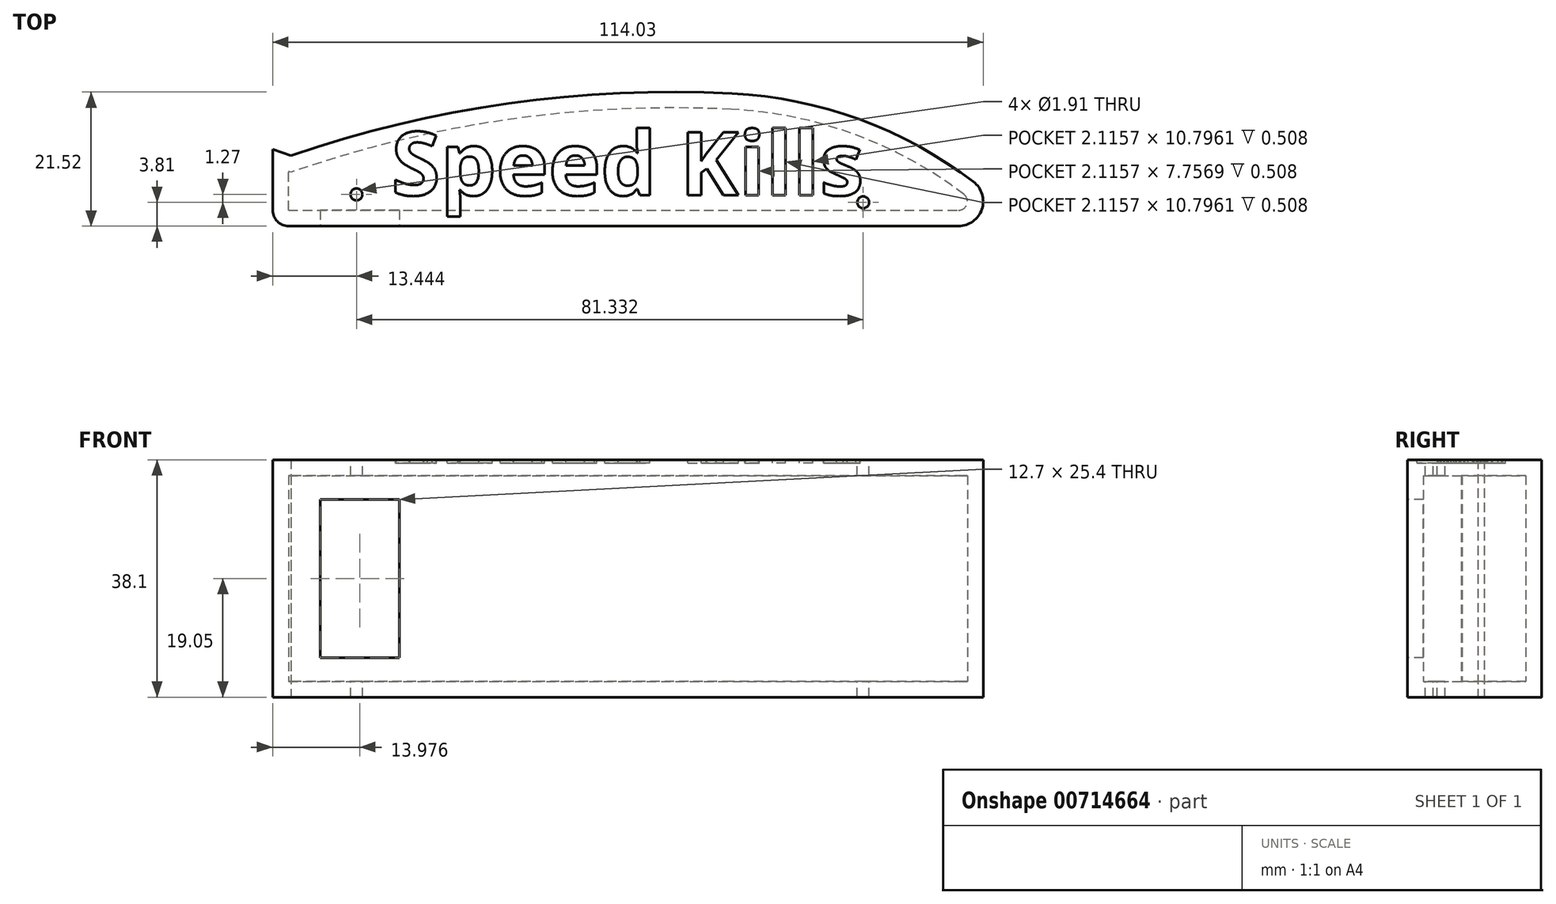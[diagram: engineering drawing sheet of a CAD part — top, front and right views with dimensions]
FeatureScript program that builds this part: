
annotation { "Feature Type Name" : "Feature", "Feature Type Description" : "" }
export const myFeature = defineFeature(function(context is Context, id is Id, definition is map)
    precondition{}
    {
        {
            var Q0;
            Q0=qCreatedBy(makeId("Top.planeOp"),FACE);
            var sketch = newSketch(context, id + "F0", { "sketchPlane" : qUnion([Q0])});
            skLineSegment(sketch, "E0", {"start": v(2.54, 0) * mm, "end": v(110.08, 0) * mm});
            skLineSegment(sketch, "E1", {"start": v(0, 2.54) * mm, "end": v(0, 10.3) * mm});
            skPoint(sketch, "E2.visualSharp", {"position": v(0, 0) * mm});
            skArc(sketch, "E2.filletArc", {"start": v(0, 2.54) * mm, "mid": v(0.74, 0.74) * mm, "end": v(2.54, 0) * mm});
            skArc(sketch, "E3", {"start": v(112.48, 7.1) * mm, "mid": v(94.19, 17.13) * mm, "end": v(73.75, 21.28) * mm});
            skArc(sketch, "E4", {"start": v(73.75, 21.28) * mm, "mid": v(36.33, 19.45) * mm, "end": v(0, 10.3) * mm});
            skArc(sketch, "E5", {"start": v(110.08, 0) * mm, "mid": v(113.83, 2.7) * mm, "end": v(112.48, 7.1) * mm});
            skSolve(sketch);
        }
        {
            var Q0;
            Q0=makeQuery(id+"F0.imprint","IMPRINT",FACE,{"disambiguationData":[TD([[makeQuery(id+"F0.imprint","IMPRINT",EDGE,{"derivedFrom":sQuery(id+"F0.wireOp",EDGE,"E0")}),1.0]])]});
            extrude(context, id + "F1", {"entities" : qUnion([Q0]), "depth" : 38.1 * mm, "offsetDistance" : 25.4 * mm});
        }
        {
            var Q0;
            Q0=makeQuery(id+"F1.opExtrude","CAP_FACE",FACE,{"disambiguationData":[OSD([sQuery(id+"F0.wireOp",EDGE,"E0"),sQuery(id+"F0.wireOp",EDGE,"E1"),sQuery(id+"F0.wireOp",EDGE,"fc349dd0-3314-4c5f-804f-7142f53e0da9"),sQuery(id+"F0.wireOp",EDGE,"E2.filletArc"),sQuery(id+"F0.wireOp",EDGE,"E3"),sQuery(id+"F0.wireOp",EDGE,"E4")])],"isStart":true});
            var sketch = newSketch(context, id + "F2", { "sketchPlane" : qUnion([Q0])});
            skLineSegment(sketch, "E6", {"start": v(0, -10.3) * mm, "end": v(0, -12.32) * mm});
            skLineSegment(sketch, "E7", {"start": v(2.9, -11.31) * mm, "end": v(0, -12.32) * mm});
            skSolve(sketch);
        }
        {
            var Q0;
            {var subQ0=sQuery(id+"F2.wireOp",EDGE,"E6");Q0=makeQuery(id+"F2.imprint","IMPRINT",FACE,{"disambiguationData":[TD([[makeQuery(id+"F2.imprint","IMPRINT",EDGE,{"derivedFrom":subQ0}),1.0]])]});}
            extrude(context, id + "F3", {"entities" : qUnion([Q0]), "operationType" : NewBodyOperationType.ADD, "oppositeDirection" : true, "depth" : 38.1 * mm, "offsetDistance" : 25.4 * mm});
        }
        {
            var Q0;
            Q0=makeQuery(id+"F1.opExtrude","SWEPT_FACE",FACE,{"disambiguationData":[OSD([sQuery(id+"F0.wireOp",EDGE,"E0")])]});
            var Q1;
            Q1=makeQuery(id+"F1.opExtrude","SWEPT_BODY",BODY,{"disambiguationData":[OSD([sQuery(id+"F0.wireOp",EDGE,"E0"),sQuery(id+"F0.wireOp",EDGE,"E1"),sQuery(id+"F0.wireOp",EDGE,"E2.filletArc"),sQuery(id+"F0.wireOp",EDGE,"E3"),sQuery(id+"F0.wireOp",EDGE,"E4"),sQuery(id+"F0.wireOp",EDGE,"E5")])]});
            shell(context, id + "F4", {"isHollow" : true, "entities" : qUnion([Q0]), "parts" : qUnion([Q1]), "thickness" : 2.54 * mm});
        }
        {
            var Q0;
            Q0=makeQuery(id+"F1.opExtrude","SWEPT_FACE",FACE,{"disambiguationData":[OSD([sQuery(id+"F0.wireOp",EDGE,"E0")])]});
            var sketch = newSketch(context, id + "F5", { "sketchPlane" : qUnion([Q0])});
            skLineSegment(sketch, "E8.bottom", {"start": v(7.63, 31.75) * mm, "end": v(20.33, 31.75) * mm});
            skLineSegment(sketch, "E8.top", {"start": v(7.63, 6.35) * mm, "end": v(20.33, 6.35) * mm});
            skLineSegment(sketch, "E8.left", {"start": v(7.63, 31.75) * mm, "end": v(7.63, 6.35) * mm});
            skLineSegment(sketch, "E8.right", {"start": v(20.33, 31.75) * mm, "end": v(20.33, 6.35) * mm});
            skSolve(sketch);
        }
        {
            var Q0;
            Q0=makeQuery(id+"F5.imprint","IMPRINT",FACE,{"disambiguationData":[TD([[makeQuery(id+"F5.imprint","IMPRINT",EDGE,{"derivedFrom":sQuery(id+"F5.wireOp",EDGE,"E8.bottom")}),-1.0]])]});
            extrude(context, id + "F6", {"entities" : qUnion([Q0]), "operationType" : NewBodyOperationType.REMOVE, "oppositeDirection" : true, "depth" : 6.35 * mm, "offsetDistance" : 25.4 * mm});
        }
        {
            var Q0;
            {var subQ0=sQuery(id+"F0.wireOp",EDGE,"E4");Q0=makeQuery(id+"F3.boolean.opBoolean","MERGE",FACE,{"derivedFrom":[makeQuery(id+"F1.opExtrude","CAP_FACE",FACE,{"disambiguationData":[OSD([sQuery(id+"F0.wireOp",EDGE,"E0"),sQuery(id+"F0.wireOp",EDGE,"E1"),sQuery(id+"F0.wireOp",EDGE,"E2.filletArc"),sQuery(id+"F0.wireOp",EDGE,"E3"),subQ0,sQuery(id+"F0.wireOp",EDGE,"E5")])],"isStart":false}),makeQuery(id+"F3.opExtrude","CAP_FACE",FACE,{"disambiguationData":[OSD([subQ0,sQuery(id+"F2.wireOp",EDGE,"E6"),sQuery(id+"F2.wireOp",EDGE,"E7")])],"isStart":false})]});}
            var sketch = newSketch(context, id + "F7", { "sketchPlane" : qUnion([Q0])});
            skPoint(sketch, "E9", {"position": v(94.78, 3.81) * mm});
            skPoint(sketch, "E9.positionSnap0", {"position": v(113.83, 3.81) * mm});
            skPoint(sketch, "E10", {"position": v(13.44, 5.08) * mm});
            skPoint(sketch, "E10.positionSnap0", {"position": v(0.74, 5.08) * mm});
            skSolve(sketch);
        }
        {
            var Q0;
            Q0=sQuery(id+"F7.wireOp",VERTEX,"E10");
            var Q1;
            Q1=sQuery(id+"F7.wireOp",VERTEX,"E9");
            var Q2;
            Q2=makeQuery(id+"F1.opExtrude","SWEPT_BODY",BODY,{"disambiguationData":[OSD([sQuery(id+"F0.wireOp",EDGE,"E0"),sQuery(id+"F0.wireOp",EDGE,"E1"),sQuery(id+"F0.wireOp",EDGE,"E2.filletArc"),sQuery(id+"F0.wireOp",EDGE,"E3"),sQuery(id+"F0.wireOp",EDGE,"E4"),sQuery(id+"F0.wireOp",EDGE,"E5")])]});
            hole(context, id + "F8", {"style" : HoleStyle.SIMPLE, "endStyle" : HoleEndStyle.THROUGH, "holeDiameter" : 1.9 * mm, "majorDiameter" : 6.35 * mm, "isTappedThrough" : true, "tappedDepth" : 12.7 * mm, "tapClearance" : 3, "locations" : qUnion([Q0, Q1]), "scope" : qUnion([Q2])});
        }
        {
            var Q0;
            {var subQ0=sQuery(id+"F0.wireOp",EDGE,"E4");Q0=makeQuery(id+"F3.boolean.opBoolean","MERGE",FACE,{"derivedFrom":[makeQuery(id+"F1.opExtrude","CAP_FACE",FACE,{"disambiguationData":[OSD([sQuery(id+"F0.wireOp",EDGE,"E0"),sQuery(id+"F0.wireOp",EDGE,"E1"),sQuery(id+"F0.wireOp",EDGE,"E2.filletArc"),sQuery(id+"F0.wireOp",EDGE,"E3"),subQ0,sQuery(id+"F0.wireOp",EDGE,"E5")])],"isStart":false}),makeQuery(id+"F3.opExtrude","CAP_FACE",FACE,{"disambiguationData":[OSD([subQ0,sQuery(id+"F2.wireOp",EDGE,"E6"),sQuery(id+"F2.wireOp",EDGE,"E7")])],"isStart":false})]});}
            var sketch = newSketch(context, id + "F9", { "sketchPlane" : qUnion([Q0])});
            skText(sketch, "E11", { "text": "Speed Kills\n", "fontName": "OpenSans-Bold.ttf"});
            const initialGuessF9  = {"E11": [0.01905, 0.00494, 1, 0, 0.01023]};
            skSetInitialGuess(sketch, initialGuessF9);
            skSolve(sketch);
        }
        {
            var Q0;
            Q0 = qSketchRegion(id + "F9", true);
            extrude(context, id + "F10", {"entities" : qUnion([Q0]), "operationType" : NewBodyOperationType.REMOVE, "oppositeDirection" : true, "depth" : 0.5 * mm, "offsetDistance" : 25.4 * mm});
        }
    });
